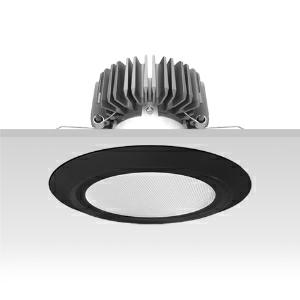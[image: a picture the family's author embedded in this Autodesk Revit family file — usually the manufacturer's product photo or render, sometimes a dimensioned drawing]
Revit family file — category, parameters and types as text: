
# Revit family: 3f_filippi_-_3f_reno_bianco_ampio_3f_filippi_-_30687_a01049_-_3f_reno_200_wh_4000-840_dali_wide___smp_bk_00fb
name_source: partatom
category: Lighting Fixtures
units: mm (PartAtom-declared; Revit-internal decimal feet)

## family parameters
Cut with Voids When Loaded = No
Host = Face
Light Source = No
Part Type = Normal
Room Calculation Point = No
Round Connector Dimension = Use Diameter
Shared = No

## types (1)
- 3F Filippi - 3F Reno Bianco Ampio (1 x LED, 3089 lm, 36 W, 4000 K)
    Apparent Load = 36 VA
    Approval mark = CE
    CIE Flux Codes = 74 92 98 100 100
    Color Rendering = 80
    Color Temperature = 4000 K
    Control Gear = Electronic transformer
    Default Elevation = 1800 mm
    Description = ILLUMINOTECHNICAL
Luminous efficiency 100% (DLOR 100%, ULOR 0%).
Initial luminous flux of the luminaire 3089 lm.
Direct symmetric wide distribution.
Installation Interdistance Transv.D = 1.06 x hu - Long.D = 1.04 x hu.
Tabular UGR (CIE 117 - 4H-8H; S=0.25H; 70/50/20): RUG 23.5 - 23.3.
Beam angle: 70° - 69°.
Luminous efficacy 86 lm/W.
Lifetime (L90/B10): 30000 h. (tq+25°C)
Lifetime (L85/B10): 50000 h. (tq+25°C)
Lifetime (L70/B10): 80000 h. (tq+25°C)
Sudden decreased luminous flux after 50000 hours: 0% (C0).
Photobiological safety in compliance with IEC/TR 62778: RG1 low risk, (IEC 62471).
In compliance with IEC/EN 62722-2-1 - IEC/EN 62717 standards.

SOURCE
Compact LED module 4000/840.
Energy efficiency class (UE 2019/2020 - UE 2019/2015): D.
CIE 13.3 Colour rendering index: CRI >80 (R9 <50%).
IES TM-30 Fidelity Index: Rf = 84 Rg = 95.
CCT nominal colour temperature 4000 K.
Colour initial tolerance (MacAdam): SDCM 3.
Zhaga Book 3 compliant.

MECHANICAL
Passive heat dissipator in die-casting aluminium, oversized, for optimum thermal management of the LED module.
Parabolic element with graduated/concentric rings in white polycarbonate.
Transparent external lens with glossy and satin differentiated surfaces, with a cooling and anti-insect system in methacrylate (PMMA).
Fastening spring clips in stainless steel.
Dimensions: diameter 226 mm, height 146 mm. Weight 1.7 kg.
IP44 protection degree for exposed part, IP20 for recessed part.
Mechanical strength to impacts IK05 (0.7 joule).
Glow-wire test resistance 650°C.

ELECTRICAL
Wiring on a separate unit.
Halogen Free DALI-2 DATI (Parts 251, 252, 253), PUSH-DIM, electronic wiring 230V-50/60Hz, power factor 0.97 at full load, THD <25%, constant output current, SELV, class II, 1 driver, 1 DALI addresse.
Power of the luminaire 36 W.
ENEC - CE.
SAFE FLICKER: PstLM=<1 and SVM=<0.4 (IEC TR 61547-1 and IEC TR 63158), to ensure a more comfortable and safe light.
Luminaire compliant with EN 60598-2-22 for power supply from a centralised emergency system CPSS (Central Power Supply System), not incorporated in the luminaire - high risk areas excluded. The default power and flux are 100% in AC and 100% in DC.
Ambient temperature from 0°C to +25°C.
Temperature class T6 max 85°C.
Relative humidity UR: <85%.

INSTALLATION
Pull-up recessed fitting.
False ceiling carving: 200 mm.
All accessories dedicated to this product are available on the Catalog and on our website www.3F-Filippi.com.

ACCESSORIES
A01049 - Anti-glare microprismatic SMP diffuser in methacrylate (PMMA), locked and in line with the trim, in black polycarbonate.

APPLICATIONS
Suitable product for food production plants (HACCP), IFS (Food Version 6), BRC (GSFS Food Version 7).
Environments: architectural, commercial, exhibition areas, transit areas, corridors, shops, display windows, service areas.
In false ceilings with narrow voids.

LIGHT MANAGEMENT
Recommended minimum setting: 10%.
The luminaire, equipped with (DALI-2 DATI) driver, can be controlled manually with 3F Easy Dim technology or automatically/manually with wired or wireless DALI/D2D control systems.
The D2D driver guarantees interoperability with other devices with the same certification by making the following information available:
Device Data (Part 251), Energy Report (Part 252), Diagnosis & Maintenance (Part 253).
In electrical systems without a regulation system (manual or automatic) and DALI bus, a suitable jumper must be made on the DA-DA terminals of the appliance.

WARNING
Luminaire designed for disposal/recycling at end-of-life.
Replaceable (LED only) light source by a professional. Replaceable control gear by a professional.
    Height = 0 mm  [stored 0 ft]
    Lamp = 1 x LED
    Lamp Light Flux = 3089 lm
    Lamp Power = 36 W
    Lamp count = 1
    Length = 226 mm
    Lifetime = 50000 h
    Luminous efficacy = 86 lm/W
    Manufacturer = 3F Filippi
    ModVariant = No
    Model = 3F Filippi - 30687+A01049 - 3F Reno 200 WH 4000-840 DALI WIDE + SMP BK
    Mounting Place = Ceiling
    Mounting Type = Recessed
    Number of Poles = 1
    OnlyDefault = Yes
    Power Factor = 1
    Product Name = 3F Filippi - 3F Reno Bianco Ampio
    Product group = recessed luminaire
    ProductGroupID = 4
    Protection Class = Protection class II
    Protection Degree = IP 20
    RLX_Detail_Level = 1
    RLX_Emergency_Light_Flux = 0 lm
    RLX_Emergency_Type = 0
    RLX_Emergency_Type_DB = No
    RlxData = <blob elided: 100321 chars, md5=fa973c78>
    Socket = socket
    Standby Power = 0 W
    System Light Flux = 3089 lm
    System Power = 36 W
    Type Comments = Product without accessories
    Type Image = 3ffilippi_3f_reno_200_bk_vs_smp.jpg
    URL = http://relux.com
    VarID = ---
    Voltage = 0 V
    Weight = 0.00 kg
    Width = 0 mm  [stored 0 ft]

note: [stored X ft] marks values corroborated as IEEE doubles in the binary element streams (Revit-internal decimal feet)

## geometry (parser evidence)
native form markers: Blend x4, Sweep x10
no freeform markers — native parametric forms only
